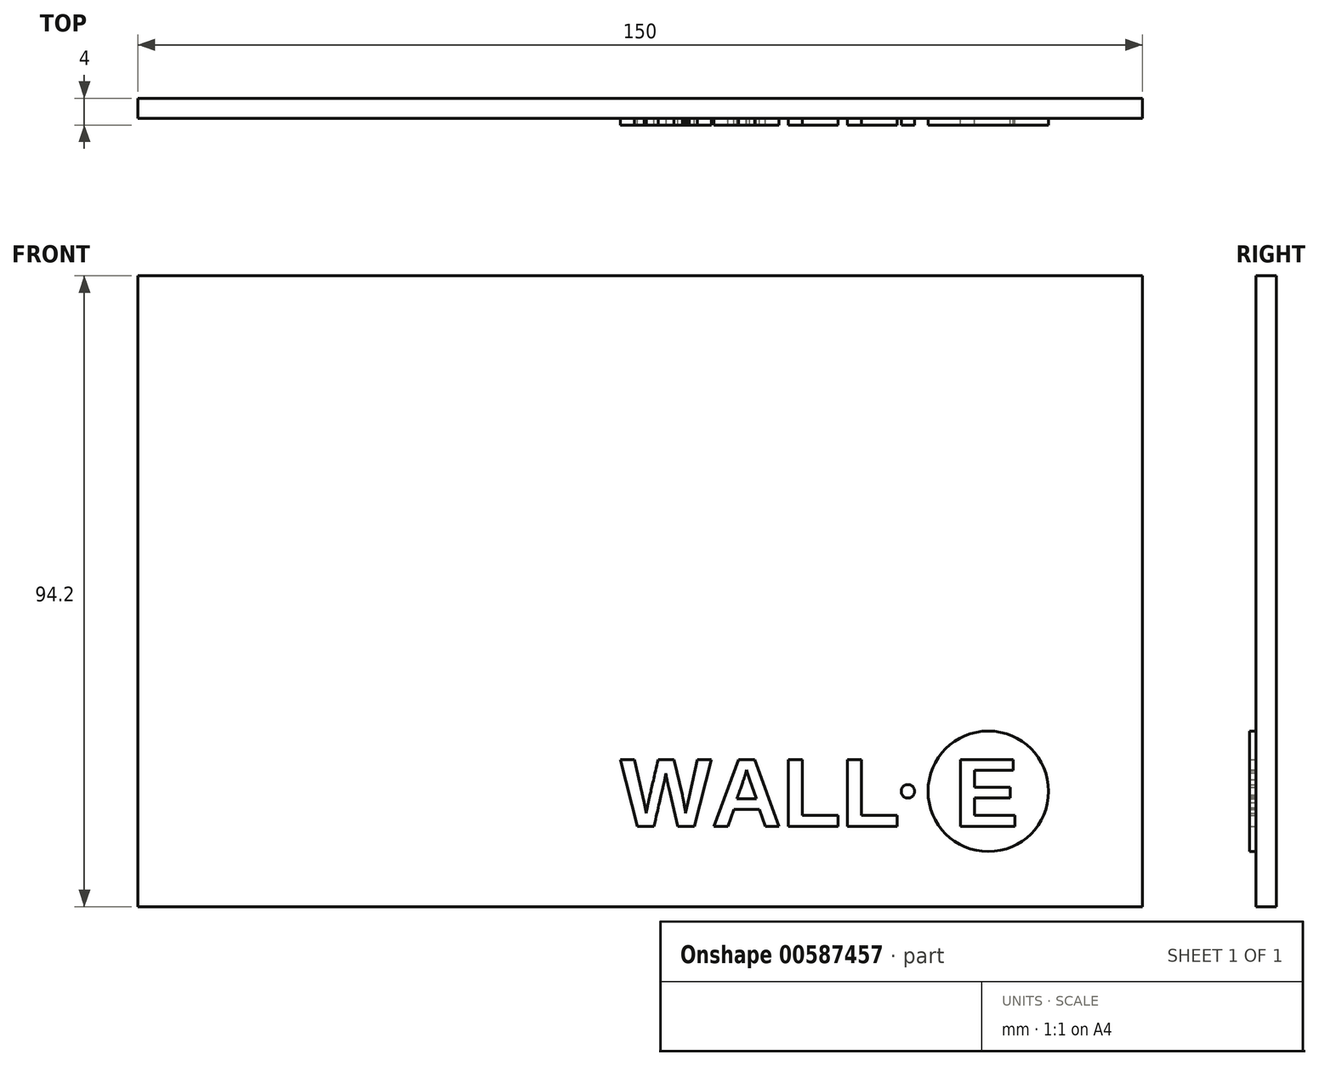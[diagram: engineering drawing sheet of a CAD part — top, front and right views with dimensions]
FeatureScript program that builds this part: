
annotation { "Feature Type Name" : "Feature", "Feature Type Description" : "" }
export const myFeature = defineFeature(function(context is Context, id is Id, definition is map)
    precondition{}
    {
        {
            var Q0;
            Q0=qCreatedBy(makeId("Front.planeOp"),FACE);
            var sketch = newSketch(context, id + "F0", { "sketchPlane" : qUnion([Q0])});
            skLineSegment(sketch, "E0", {"start": v(-75, 47.1) * mm, "end": v(-75, -47.1) * mm});
            skLineSegment(sketch, "E1", {"start": v(-75, -47.1) * mm, "end": v(75, -47.1) * mm});
            skLineSegment(sketch, "E2", {"start": v(75, -47.1) * mm, "end": v(75, 47.1) * mm});
            skLineSegment(sketch, "E3", {"start": v(75, 47.1) * mm, "end": v(-75, 47.1) * mm});
            skSolve(sketch);
        }
        {
            var Q0;
            Q0 = qSketchRegion(id + "F0", true);
            extrude(context, id + "F1", {"entities" : qUnion([Q0]), "depth" : 3 * mm, "offsetDistance" : 25 * mm});
        }
        {
            var Q0;
            Q0=makeQuery(id+"F1.opExtrude","CAP_FACE",FACE,{"disambiguationData":[OSD([sQuery(id+"F0.wireOp",EDGE,"E0"),sQuery(id+"F0.wireOp",EDGE,"E1"),sQuery(id+"F0.wireOp",EDGE,"E2"),sQuery(id+"F0.wireOp",EDGE,"E3")])],"isStart":false});
            var sketch = newSketch(context, id + "F2", { "sketchPlane" : qUnion([Q0])});
            skText(sketch, "E4", { "text": "WALL  E", "fontName": "Arimo-Bold.ttf"});
            skCircle(sketch, "E5", {"center": v(52, -29.88) * mm, "radius": 9 * mm});
            skPoint(sketch, "E5.centerSnap0", {"position": v(57, -29.88) * mm});
            skCircle(sketch, "E6", {"center": v(40, -29.88) * mm, "radius": 1 * mm});
            const initialGuessF2  = {"E4": [-0.003, -0.0351, 1, 0, 0.01043]};
            skSetInitialGuess(sketch, initialGuessF2);
            skSolve(sketch);
        }
        {
            var Q0;
            Q0 = qSketchRegion(id + "F2", true);
            extrude(context, id + "F3", {"entities" : qUnion([Q0]), "operationType" : NewBodyOperationType.ADD, "depth" : 1 * mm, "offsetDistance" : 25 * mm});
        }
    });
